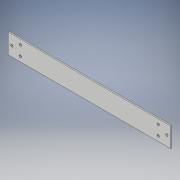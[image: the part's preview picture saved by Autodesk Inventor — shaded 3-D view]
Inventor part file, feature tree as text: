
AUTODESK INVENTOR PART (.ipt)
format: ipt  version: 2017 (Build 210142000, 142)  size: 107,520 bytes
history: native  units: in
note: dims shown in document units (in); Inventor stores cm internally (conversion verified against a paired STEP export)
features: extrude x1
ambient origin geometry x8: Origin, YZ Plane, XZ Plane, XY Plane, X Axis, Y Axis, Z Axis, Center Point
bodies: Body1 (feature_tree)
feature tree (1):
  extrude  "Extrusion2"  Depth=16.5in
